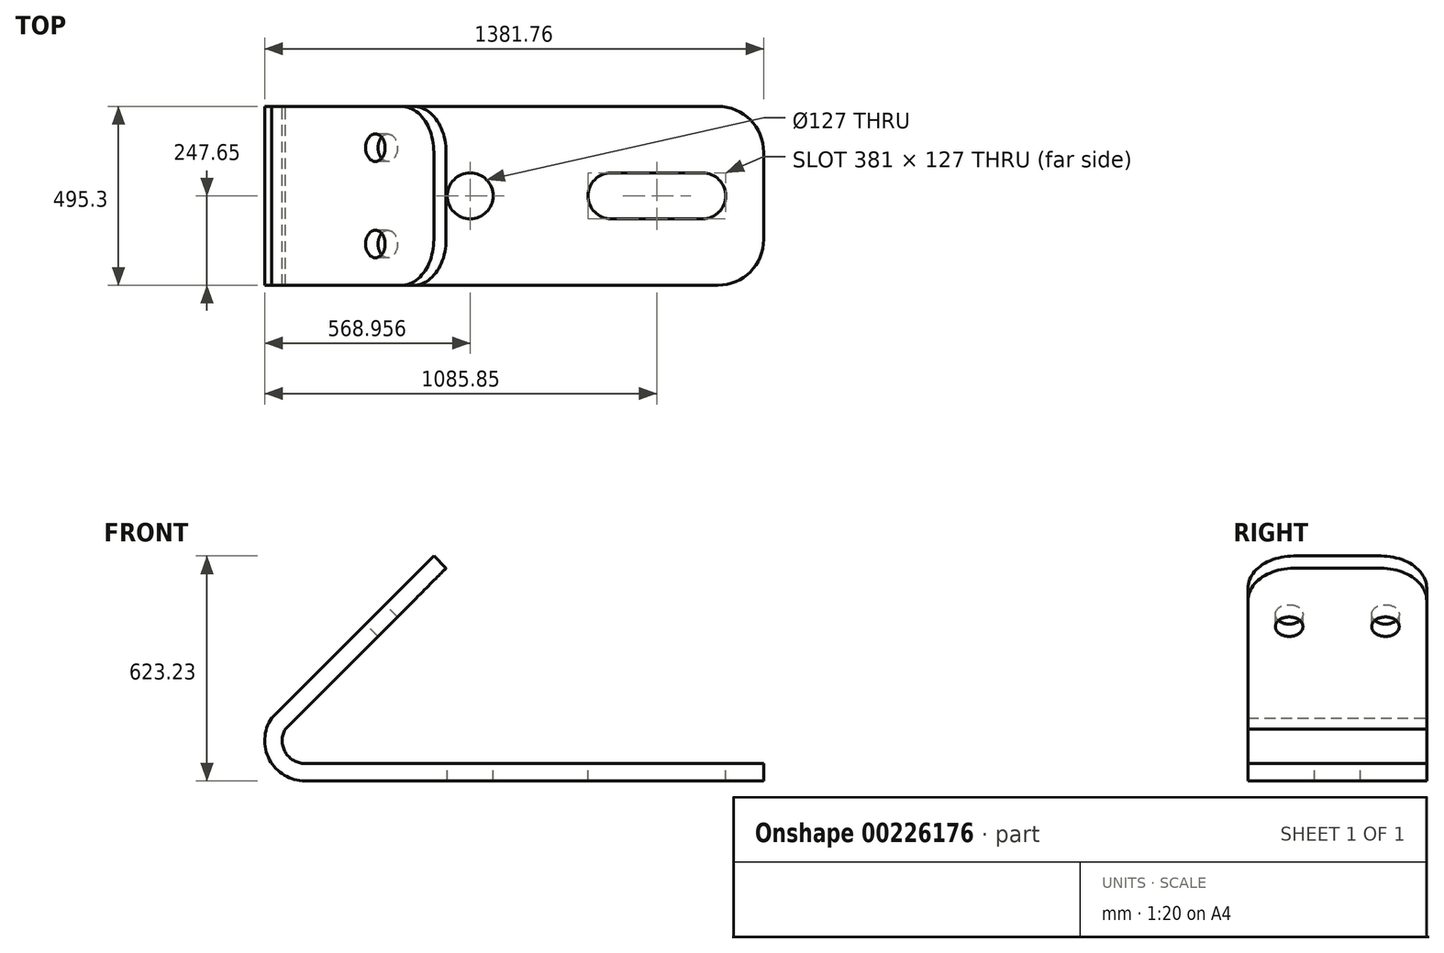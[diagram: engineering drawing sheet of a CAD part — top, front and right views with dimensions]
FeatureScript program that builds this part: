
annotation { "Feature Type Name" : "Feature", "Feature Type Description" : "" }
export const myFeature = defineFeature(function(context is Context, id is Id, definition is map)
    precondition{}
    {
        {
            var Q0;
            Q0=qCreatedBy(makeId("Front.planeOp"),FACE);
            var sketch = newSketch(context, id + "F0", { "sketchPlane" : qUnion([Q0])});
            skLineSegment(sketch, "E0", {"start": v(-619.91, 0) * mm, "end": v(650.09, 0) * mm});
            skLineSegment(sketch, "E1", {"start": v(650.09, 0) * mm, "end": v(650.09, 48.26) * mm});
            skLineSegment(sketch, "E2", {"start": v(650.09, 48.26) * mm, "end": v(-619.91, 48.26) * mm});
            skArc(sketch, "E3", {"start": v(-619.91, 0) * mm, "mid": v(-718.58, 59.27) * mm, "end": v(-712.6, 174.22) * mm});
            skLineSegment(sketch, "E4", {"start": v(-712.6, 174.22) * mm, "end": v(-263.58, 623.23) * mm});
            skLineSegment(sketch, "E5", {"start": v(-263.58, 623.23) * mm, "end": v(-229.45, 589.1) * mm});
            skLineSegment(sketch, "E6", {"start": v(-229.45, 589.1) * mm, "end": v(-678.47, 140.1) * mm});
            skArc(sketch, "E7", {"start": v(-619.91, 48.26) * mm, "mid": v(-675, 80.18) * mm, "end": v(-674.7, 143.85) * mm});
            skSolve(sketch);
        }
        {
            var Q0;
            Q0=makeQuery(id+"F0.imprint","IMPRINT",FACE,{"disambiguationData":[TD([[makeQuery(id+"F0.imprint","IMPRINT",EDGE,{"derivedFrom":sQuery(id+"F0.wireOp",EDGE,"E0")}),1.0]])]});
            extrude(context, id + "F1", {"entities" : qUnion([Q0]), "endBound" : BoundingType.SYMMETRIC, "depth" : 495.3 * mm});
        }
        {
            var Q0;
            Q0=makeQuery(id+"F1.opExtrude","SWEPT_FACE",FACE,{"disambiguationData":[OSD([sQuery(id+"F0.wireOp",EDGE,"E2")])]});
            var sketch = newSketch(context, id + "F2", { "sketchPlane" : qUnion([Q0])});
            skLineSegment(sketch, "E8", {"start": v(650.09, 0) * mm, "end": v(-162.71, 0) * mm, "construction": true});
            skPoint(sketch, "E8.endSnap0", {"position": v(650.09, 0) * mm});
            skCircle(sketch, "E9", {"center": v(-162.71, 0) * mm, "radius": 63.5 * mm});
            skLineSegment(sketch, "E10.bottom", {"start": v(481.18, -63.5) * mm, "end": v(227.18, -63.5) * mm});
            skLineSegment(sketch, "E10.top", {"start": v(481.18, 63.5) * mm, "end": v(227.18, 63.5) * mm});
            skLineSegment(sketch, "E10.left", {"start": v(481.18, -63.5) * mm, "end": v(481.18, 63.5) * mm});
            skLineSegment(sketch, "E10.right", {"start": v(227.18, -63.5) * mm, "end": v(227.18, 63.5) * mm});
            skPoint(sketch, "E10.middle", {"position": v(354.18, 0) * mm});
            skArc(sketch, "E11", {"start": v(227.18, 63.5) * mm, "mid": v(163.68, 0) * mm, "end": v(227.18, -63.5) * mm});
            skArc(sketch, "E12", {"start": v(481.18, -63.5) * mm, "mid": v(544.68, 0) * mm, "end": v(481.18, 63.5) * mm});
            skSolve(sketch);
        }
        {
            var Q0;
            Q0=makeQuery(id+"F2.imprint","IMPRINT",FACE,{"disambiguationData":[TD([[makeQuery(id+"F2.imprint","IMPRINT",EDGE,{"derivedFrom":sQuery(id+"F2.wireOp",EDGE,"E9")}),1.0]])]});
            extrude(context, id + "F3", {"entities" : qUnion([Q0]), "operationType" : NewBodyOperationType.REMOVE, "endBound" : BoundingType.THROUGH_ALL, "oppositeDirection" : true, "depth" : 25.4 * mm});
        }
        {
            var Q0;
            Q0=makeQuery(id+"F2.imprint","IMPRINT",FACE,{"disambiguationData":[TD([[makeQuery(id+"F2.imprint","IMPRINT",EDGE,{"derivedFrom":sQuery(id+"F2.wireOp",EDGE,"E10.bottom")}),-1.0]])]});
            var Q1;
            Q1=makeQuery(id+"F2.imprint","IMPRINT",FACE,{"disambiguationData":[TD([[makeQuery(id+"F2.imprint","IMPRINT",EDGE,{"derivedFrom":sQuery(id+"F2.wireOp",EDGE,"E10.right")}),1.0]])]});
            var Q2;
            Q2=makeQuery(id+"F2.imprint","IMPRINT",FACE,{"disambiguationData":[TD([[makeQuery(id+"F2.imprint","IMPRINT",EDGE,{"derivedFrom":sQuery(id+"F2.wireOp",EDGE,"E10.left")}),-1.0]])]});
            extrude(context, id + "F4", {"entities" : qUnion([Q0, Q1, Q2]), "operationType" : NewBodyOperationType.REMOVE, "endBound" : BoundingType.THROUGH_ALL, "oppositeDirection" : true, "depth" : 25.4 * mm});
        }
        {
            var Q0;
            Q0=makeQuery(id+"F1.opExtrude","SWEPT_FACE",FACE,{"disambiguationData":[OSD([sQuery(id+"F0.wireOp",EDGE,"E4")])]});
            var sketch = newSketch(context, id + "F5", { "sketchPlane" : qUnion([Q0])});
            skLineSegment(sketch, "E13", {"start": v(-133.35, -380.69) * mm, "end": v(-133.35, 254.31) * mm, "construction": true});
            skLineSegment(sketch, "E14", {"start": v(133.35, -380.69) * mm, "end": v(133.35, 254.31) * mm, "construction": true});
            skCircle(sketch, "E15", {"center": v(133.35, 25.71) * mm, "radius": 38.1 * mm});
            skCircle(sketch, "E16", {"center": v(-133.35, 25.71) * mm, "radius": 38.1 * mm});
            skSolve(sketch);
        }
        {
            var Q0;
            Q0=makeQuery(id+"F5.imprint","IMPRINT",FACE,{"disambiguationData":[TD([[makeQuery(id+"F5.imprint","IMPRINT",EDGE,{"derivedFrom":sQuery(id+"F5.wireOp",EDGE,"E15")}),1.0]])]});
            extrude(context, id + "F6", {"entities" : qUnion([Q0]), "operationType" : NewBodyOperationType.REMOVE, "oppositeDirection" : true, "depth" : 218.44 * mm});
        }
        {
            var Q0;
            Q0=makeQuery(id+"F5.imprint","IMPRINT",FACE,{"disambiguationData":[TD([[makeQuery(id+"F5.imprint","IMPRINT",EDGE,{"derivedFrom":sQuery(id+"F5.wireOp",EDGE,"E16")}),1.0]])]});
            extrude(context, id + "F7", {"entities" : qUnion([Q0]), "operationType" : NewBodyOperationType.REMOVE, "oppositeDirection" : true, "depth" : 218.44 * mm});
        }
        {
            var Q0;
            Q0=makeQuery(id+"F1.opExtrude","CAP_EDGE",EDGE,{"disambiguationData":[OSD([sQuery(id+"F0.wireOp",EDGE,"E1")])],"isStart":false});
            var Q1;
            Q1=makeQuery(id+"F1.opExtrude","CAP_EDGE",EDGE,{"disambiguationData":[OSD([sQuery(id+"F0.wireOp",EDGE,"E1")])],"isStart":true});
            var Q2;
            Q2=makeQuery(id+"F1.opExtrude","CAP_EDGE",EDGE,{"disambiguationData":[OSD([sQuery(id+"F0.wireOp",EDGE,"E5")])],"isStart":false});
            var Q3;
            Q3=makeQuery(id+"F1.opExtrude","CAP_EDGE",EDGE,{"disambiguationData":[OSD([sQuery(id+"F0.wireOp",EDGE,"E5")])],"isStart":true});
            fillet(context, id + "F8", {"entities" : qUnion([Q0, Q1, Q2, Q3]), "radius" : 127 * mm, "tangentPropagation" : true, "allowEdgeOverflow" : false});
        }
    });
